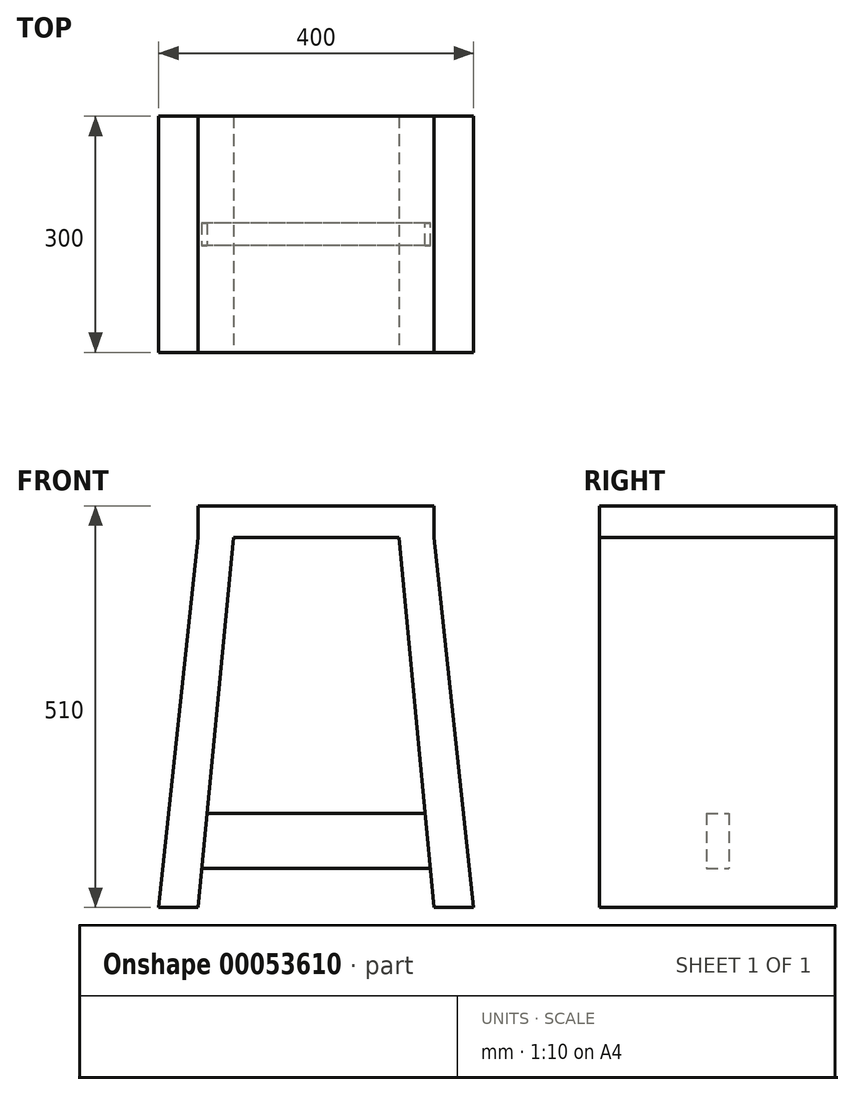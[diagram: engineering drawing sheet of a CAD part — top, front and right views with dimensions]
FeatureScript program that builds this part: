
annotation { "Feature Type Name" : "Feature", "Feature Type Description" : "" }
export const myFeature = defineFeature(function(context is Context, id is Id, definition is map)
    precondition{}
    {
        {
            var Q0;
            Q0=qCreatedBy(makeId("Top.planeOp"),FACE);
            var sketch = newSketch(context, id + "F0", { "sketchPlane" : qUnion([Q0])});
            skLineSegment(sketch, "E0.rect.bottom", {"start": v(150, 150) * mm, "end": v(-150, 150) * mm});
            skLineSegment(sketch, "E0.rect.top", {"start": v(150, -150) * mm, "end": v(-150, -150) * mm});
            skLineSegment(sketch, "E0.rect.left", {"start": v(150, 150) * mm, "end": v(150, -150) * mm});
            skLineSegment(sketch, "E0.rect.right", {"start": v(-150, 150) * mm, "end": v(-150, -150) * mm});
            skPoint(sketch, "E0.rect.middle", {"position": v(0, 0) * mm});
            skSolve(sketch);
        }
        {
            var Q0;
            Q0=makeQuery(id+"F0.imprint","IMPRINT",FACE,{"disambiguationData":[TD([[makeQuery(id+"F0.imprint","IMPRINT",EDGE,{"derivedFrom":sQuery(id+"F0.wireOp",EDGE,"E0.rect.bottom")}),1.0]])]});
            extrude(context, id + "F1", {"entities" : qUnion([Q0]), "depth" : 40 * mm});
        }
        {
            var Q0;
            Q0=makeQuery(id+"F1.opExtrude","CAP_FACE",FACE,{"disambiguationData":[OSD([sQuery(id+"F0.wireOp",EDGE,"E0.rect.bottom"),sQuery(id+"F0.wireOp",EDGE,"E0.rect.top"),sQuery(id+"F0.wireOp",EDGE,"E0.rect.left"),sQuery(id+"F0.wireOp",EDGE,"E0.rect.right")])],"isStart":true});
            cPlane(context, id + "F2", {"entities" : qUnion([Q0]), "cplaneType" : CPlaneType.OFFSET, "offset" : 470 * mm, "width" : 150 * mm, "height" : 150 * mm});
        }
        {
            var Q0;
            Q0=qCreatedBy(id+"F2.planeOp",FACE);
            var sketch = newSketch(context, id + "F3", { "sketchPlane" : qUnion([Q0])});
            skLineSegment(sketch, "E1.0", {"start": v(150, -150) * mm, "end": v(150, 150) * mm});
            skLineSegment(sketch, "E2", {"start": v(150, 150) * mm, "end": v(150, 150) * mm});
            skLineSegment(sketch, "E3", {"start": v(150, 150) * mm, "end": v(150, -150) * mm});
            skLineSegment(sketch, "E4", {"start": v(150, -150) * mm, "end": v(150, -150) * mm});
            skLineSegment(sketch, "E5.bottom", {"start": v(150, 150) * mm, "end": v(200, 150) * mm});
            skLineSegment(sketch, "E5.top", {"start": v(150, -150) * mm, "end": v(200, -150) * mm});
            skLineSegment(sketch, "E5.right", {"start": v(200, 150) * mm, "end": v(200, -150) * mm});
            skSolve(sketch);
        }
        {
            var Q0;
            Q0=makeQuery(id+"F1.opExtrude","CAP_FACE",FACE,{"disambiguationData":[OSD([sQuery(id+"F0.wireOp",EDGE,"E0.rect.bottom"),sQuery(id+"F0.wireOp",EDGE,"E0.rect.top"),sQuery(id+"F0.wireOp",EDGE,"E0.rect.left"),sQuery(id+"F0.wireOp",EDGE,"E0.rect.right")])],"isStart":true});
            var sketch = newSketch(context, id + "F4", { "sketchPlane" : qUnion([Q0])});
            skLineSegment(sketch, "E6.bottom", {"start": v(150, -150) * mm, "end": v(105, -150) * mm});
            skLineSegment(sketch, "E6.top", {"start": v(150, 150) * mm, "end": v(105, 150) * mm});
            skLineSegment(sketch, "E6.left", {"start": v(150, -150) * mm, "end": v(150, 150) * mm});
            skLineSegment(sketch, "E6.right", {"start": v(105, -150) * mm, "end": v(105, 150) * mm});
            skSolve(sketch);
        }
        {
            var Q1;
            Q1 = qSketchRegion(id + "F4", true);
            var Q2;
            Q2 = qSketchRegion(id + "F3", true);
            loft(context, id + "F5", {"sheetProfilesArray" : [{ "sheetProfileEntities" : qUnion([Q1]) }, { "sheetProfileEntities" : qUnion([Q2]) }]});
        }
        {
            var Q0;
            Q0=makeQuery(id+"F5.opLoft","SWEPT_BODY",BODY,{"disambiguationData":[OSD([makeQuery(id+"F3.imprint","IMPRINT",FACE,{"disambiguationData":[TD([[makeQuery(id+"F3.imprint","IMPRINT",EDGE,{"derivedFrom":sQuery(id+"F3.wireOp",EDGE,"E1.0")}),-1.0]])]}),makeQuery(id+"F4.imprint","IMPRINT",FACE,{"disambiguationData":[TD([[makeQuery(id+"F4.imprint","IMPRINT",EDGE,{"derivedFrom":sQuery(id+"F4.wireOp",EDGE,"E6.bottom")}),-1.0]])]})])]});
            var Q1;
            Q1=qCreatedBy(makeId("Right.planeOp"),FACE);
            mirror(context, id + "F6", {"operationType" : NewBodyOperationType.ADD, "entities" : qUnion([Q0]), "mirrorPlane" : qUnion([Q1])});
        }
        {
            var Q0;
            Q0=qCreatedBy(makeId("Right.planeOp"),FACE);
            var sketch = newSketch(context, id + "F7", { "sketchPlane" : qUnion([Q0])});
            skLineSegment(sketch, "E7.rect.bottom", {"start": v(-14.33, -350.46) * mm, "end": v(14.33, -350.46) * mm});
            skLineSegment(sketch, "E7.rect.top", {"start": v(-14.33, -420.73) * mm, "end": v(14.33, -420.73) * mm});
            skLineSegment(sketch, "E7.rect.left", {"start": v(-14.33, -350.46) * mm, "end": v(-14.33, -420.73) * mm});
            skLineSegment(sketch, "E7.rect.right", {"start": v(14.33, -350.46) * mm, "end": v(14.33, -420.73) * mm});
            skPoint(sketch, "E7.rect.middle", {"position": v(0, -385.6) * mm});
            skSolve(sketch);
        }
        {
            var Q0;
            Q0 = qSketchRegion(id + "F7", true);
            var Q1;
            Q1=makeQuery(id+"F5.opLoft","SWEPT_FACE",FACE,{"disambiguationData":[OSD([sQuery(id+"F0.wireOp",EDGE,"E0.rect.bottom"),sQuery(id+"F0.wireOp",EDGE,"E0.rect.top"),sQuery(id+"F3.wireOp",EDGE,"E1.0"),sQuery(id+"F3.wireOp",EDGE,"E2"),sQuery(id+"F3.wireOp",EDGE,"E4"),sQuery(id+"F4.wireOp",EDGE,"E6.bottom"),sQuery(id+"F4.wireOp",EDGE,"E6.top"),sQuery(id+"F4.wireOp",EDGE,"E6.right")])]});
            var Q2;
            Q2=makeQuery(id+"F6.opPattern","COPY",FACE,{"derivedFrom":makeQuery(id+"F5.opLoft","SWEPT_FACE",FACE,{"disambiguationData":[OSD([sQuery(id+"F0.wireOp",EDGE,"E0.rect.bottom"),sQuery(id+"F0.wireOp",EDGE,"E0.rect.top"),sQuery(id+"F3.wireOp",EDGE,"E1.0"),sQuery(id+"F3.wireOp",EDGE,"E2"),sQuery(id+"F3.wireOp",EDGE,"E4"),sQuery(id+"F4.wireOp",EDGE,"E6.bottom"),sQuery(id+"F4.wireOp",EDGE,"E6.top"),sQuery(id+"F4.wireOp",EDGE,"E6.right")])]}),"instanceName":"1"});
            extrude(context, id + "F8", {"entities" : qUnion([Q0]), "operationType" : NewBodyOperationType.ADD, "endBound" : BoundingType.UP_TO_SURFACE, "endBoundEntityFace" : qUnion([Q1]), "depth" : 25 * mm, "hasSecondDirection" : true, "secondDirectionBound" : SecondDirectionBoundingType.UP_TO_SURFACE, "secondDirectionOppositeDirection" : true, "secondDirectionBoundEntityFace" : qUnion([Q2]), "secondDirectionDepth" : 25 * mm});
        }
    });
